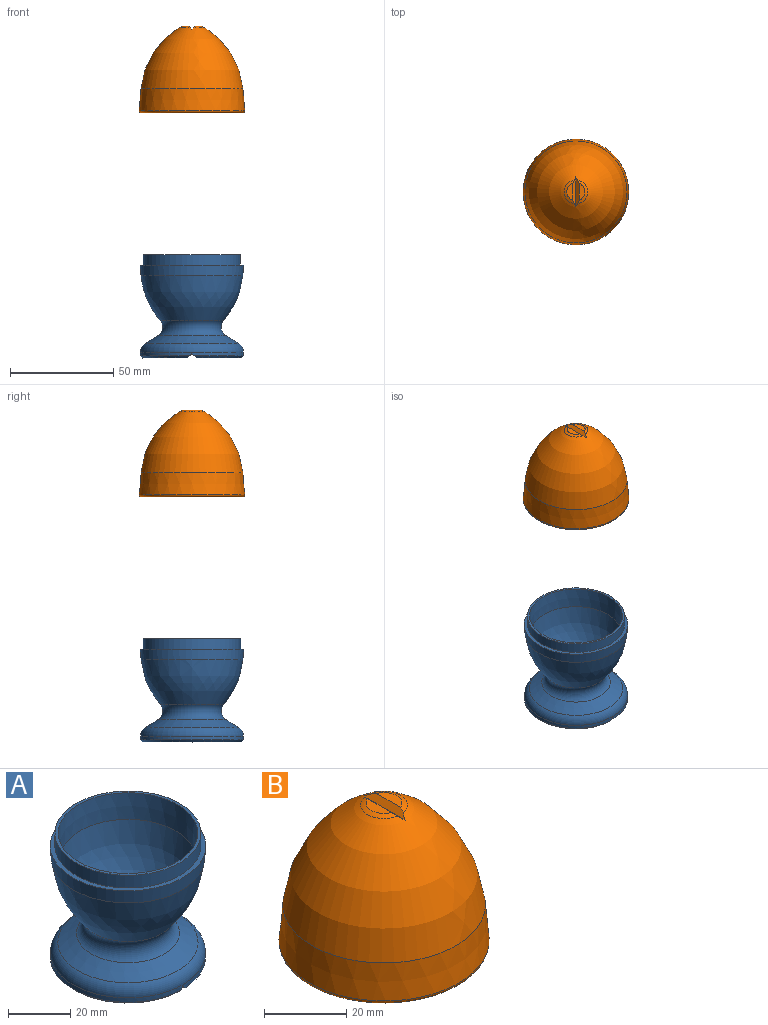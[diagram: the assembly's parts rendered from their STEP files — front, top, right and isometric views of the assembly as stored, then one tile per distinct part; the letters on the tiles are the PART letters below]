
ASSEMBLY  parts=2 mates=1
PART A: 19 faces, bbox 54x54x50.8 mm
  f0: cone r=23.95mm half-angle=45deg, axis (0,0,1), area 104.4mm2, adj f1,f5,f17
  f1: plane 47.74x21.95mm, normal (0,0,-1), area 805.4mm2, adj f0,f17
  f2: torus R=19.17mm, axis (0,0,-1), area 810.7mm2, adj f3,f16
  f3: cone r=16.57mm half-angle=58.6deg, axis (0,0,-1), area 862.7mm2, adj f2,f4
  f4: torus R=19.95mm, axis (0,0,-1), area 775mm2, adj f3,f5
  f5: cylinder r=24.95mm len=49.9mm, axis (0,0,-1), area 271mm2, adj f0,f4,f6,f17,f18
  f6: cone r=23.95mm half-angle=45deg, axis (0,0,1), area 104.4mm2, adj f5,f7,f18
  f7: plane 47.74x21.95mm, normal (0,0,-1), area 805.4mm2, adj f6,f18
  f8: plane 7.82x7.82mm, normal (0,0,1), area 48mm2, adj f9
  f9: torus R=3.91mm, axis (0,0,-1), area 356.4mm2, adj f8,f10
  f10: revolved ~43.28x43.28mm, area 2814.5mm2, adj f9,f11
  f11: cone r=21.64mm half-angle=5deg, axis (0,0,1), area 1370.9mm2, adj f10,f12
  f12: plane 47x47mm, normal (0,0,1), area 144.5mm2, adj f11,f13
  f13: cylinder r=23.5mm len=47mm, axis (0,0,-1), area 738.3mm2, adj f12,f14
  f14: plane 50.15x50.15mm, normal (0,0,1), area 240.2mm2, adj f13,f15
  f15: cone r=24.63mm half-angle=5deg, axis (0,0,1), area 801mm2, adj f14,f16
  f16: revolved ~49.25x49.25mm, area 3183.6mm2, adj f2,f15
  f17: plane 49.92x2.02mm, normal (-0.71,0,-0.71), area 139.6mm2, adj f0,f1,f5,f18
  f18: plane 49.92x2.02mm, normal (0.71,0,-0.71), area 139.6mm2, adj f5,f6,f7,f17
PART B: 16 faces, bbox 55.4x55.4x42.1 mm
  f0: torus R=1.71mm, axis (0,0,1), area 19.4mm2, adj f1,f14,f15
  f1: revolved ~48.58x48.58mm, area 8071.7mm2, adj f0,f2,f11,f13,f14
  f2: torus R=1.71mm, axis (0,0,1), area 19.4mm2, adj f1,f12,f13
  f3: plane 1.78x1.78mm, normal (0,0,-1), area 2.5mm2, adj f4
  f4: torus R=0.89mm, axis (0,0,1), area 84mm2, adj f3,f5
  f5: revolved ~43.28x43.28mm, area 3174.9mm2, adj f4,f6
  f6: cone r=21.64mm half-angle=5deg, axis (0,0,-1), area 755.6mm2, adj f5,f7
  f7: plane 47.1x47.1mm, normal (0,0,-1), area 205.5mm2, adj f6,f8
  f8: cylinder r=23.55mm len=47.1mm, axis (0,0,1), area 887.8mm2, adj f7,f9
  f9: plane 49.13x49.13mm, normal (0,0,-1), area 153mm2, adj f8,f10
  f10: torus R=24.56mm, axis (0,0,1), area 262.7mm2, adj f9,f11
  f11: cone r=24.63mm half-angle=5deg, axis (0,0,-1), area 1685.5mm2, adj f1,f10
  f12: plane 8.18x2.83mm, normal (0,0,1), area 16.8mm2, adj f2,f13
  f13: plane 14.6x1.66mm, normal (0.71,0,0.71), area 25.6mm2, adj f1,f2,f12,f14
  f14: plane 14.6x1.66mm, normal (-0.71,0,0.71), area 25.6mm2, adj f0,f1,f13,f15
  f15: plane 8.18x2.83mm, normal (0,0,1), area 16.8mm2, adj f0,f14
PLACE A t=(-33.64,-66.24,0.69)mm
PLACE B t=(-33.64,-66.24,107.79)mm
MATE slider A.f0 <-> B.f0  axis (0,0,1) through (-33.64,-66.24,30.69)mm
